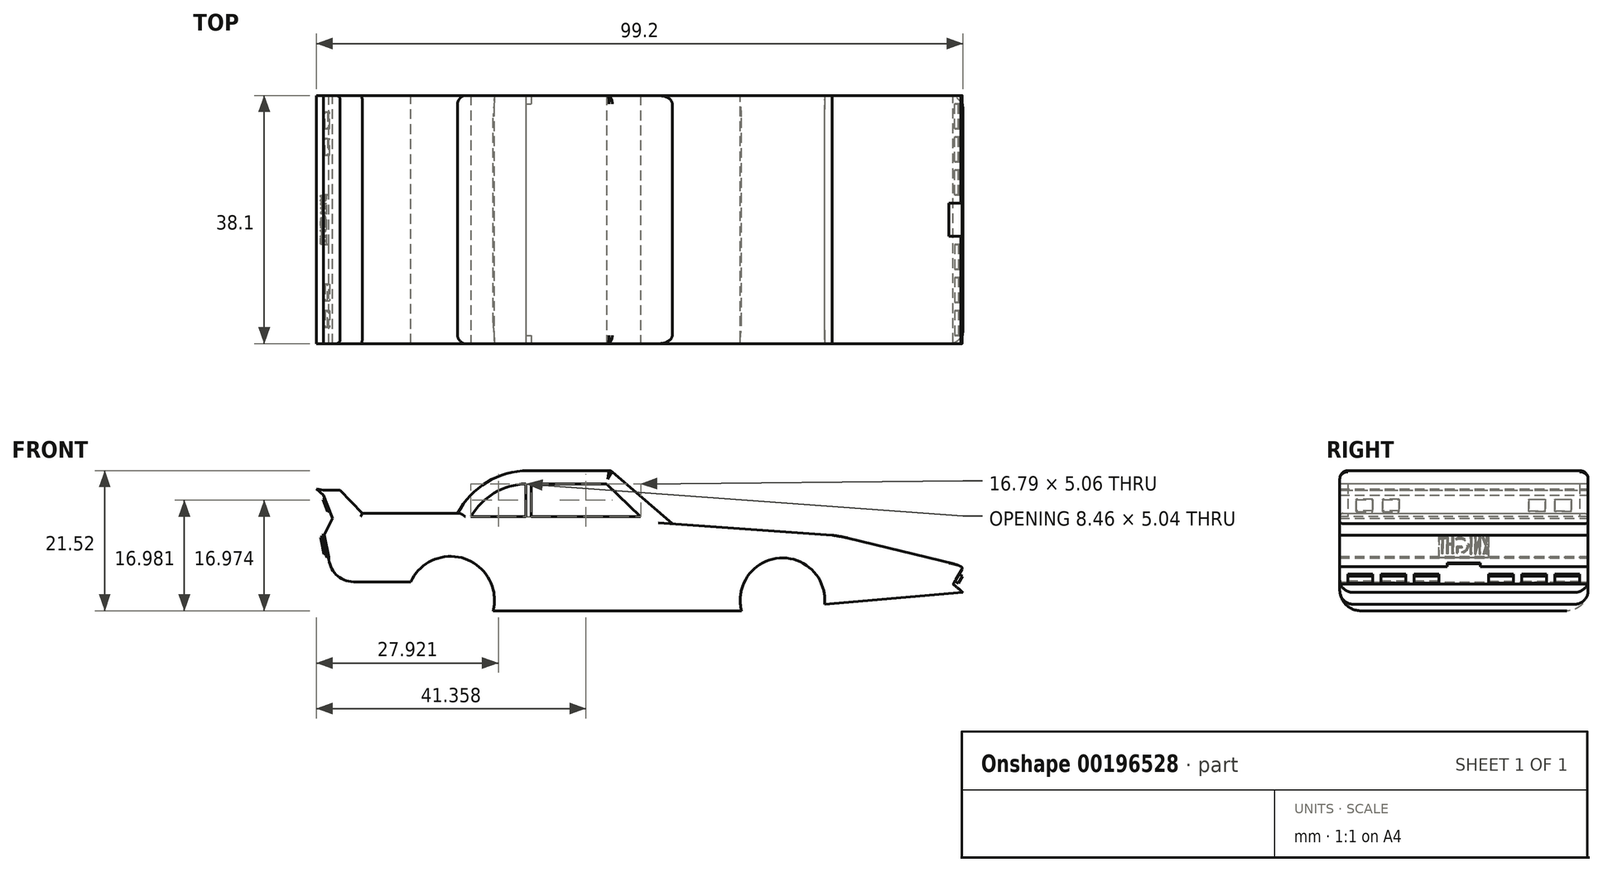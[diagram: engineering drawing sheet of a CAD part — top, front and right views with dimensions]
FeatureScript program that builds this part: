
annotation { "Feature Type Name" : "Feature", "Feature Type Description" : "" }
export const myFeature = defineFeature(function(context is Context, id is Id, definition is map)
    precondition{}
    {
        {
            var Q0;
            Q0=qCreatedBy(makeId("Front.planeOp"),FACE);
            var sketch = newSketch(context, id + "F0", { "sketchPlane" : qUnion([Q0])});
            skArc(sketch, "E0", {"start": v(4.2, 1) * mm, "mid": v(-2.78, 8.1) * mm, "end": v(-8.56, 0) * mm});
            skLineSegment(sketch, "E1", {"start": v(-8.56, 0) * mm, "end": v(-46.66, 0) * mm});
            skArc(sketch, "E2", {"start": v(-46.66, 0) * mm, "mid": v(-50.95, 7.97) * mm, "end": v(-59.3, 4.46) * mm});
            skLineSegment(sketch, "E3", {"start": v(-59.3, 4.46) * mm, "end": v(-68.07, 4.46) * mm});
            skLineSegment(sketch, "E4", {"start": v(-71.88, 8.27) * mm, "end": v(-72.57, 11.67) * mm});
            skLineSegment(sketch, "E5", {"start": v(-72.7, 18.5) * mm, "end": v(-70.16, 18.5) * mm});
            skLineSegment(sketch, "E6", {"start": v(-70.16, 18.5) * mm, "end": v(-66.76, 14.96) * mm});
            skLineSegment(sketch, "E7", {"start": v(-66.76, 14.96) * mm, "end": v(-52.11, 14.96) * mm});
            skLineSegment(sketch, "E8", {"start": v(-41.3, 21.52) * mm, "end": v(-28.6, 21.52) * mm});
            skArc(sketch, "E9", {"start": v(-41.3, 21.52) * mm, "mid": v(-47.62, 19.75) * mm, "end": v(-52.11, 14.96) * mm});
            skLineSegment(sketch, "E10", {"start": v(-28.6, 21.52) * mm, "end": v(-19.19, 13.37) * mm});
            skLineSegment(sketch, "E11", {"start": v(-19.19, 13.37) * mm, "end": v(5.34, 11.62) * mm});
            skLineSegment(sketch, "E12", {"start": v(5.34, 11.62) * mm, "end": v(25.42, 6.72) * mm});
            skLineSegment(sketch, "E13", {"start": v(25.42, 2.81) * mm, "end": v(4.2, 1) * mm});
            skLineSegment(sketch, "E14", {"start": v(25.42, 6.72) * mm, "end": v(23.91, 4.1) * mm});
            skLineSegment(sketch, "E15", {"start": v(23.91, 4.1) * mm, "end": v(25.42, 2.81) * mm});
            skPoint(sketch, "E16.visualSharp", {"position": v(-71.88, 4.46) * mm});
            skArc(sketch, "E16.filletArc", {"start": v(-71.88, 8.27) * mm, "mid": v(-70.77, 5.57) * mm, "end": v(-68.07, 4.46) * mm});
            skPoint(sketch, "E17.orphan", {"position": v(-59.72, 0) * mm});
            skPoint(sketch, "E18.orphan", {"position": v(4.02, 0) * mm});
            skLineSegment(sketch, "E19", {"start": v(-72.7, 18.5) * mm, "end": v(-73.78, 18.73) * mm});
            skLineSegment(sketch, "E20", {"start": v(-73.78, 18.73) * mm, "end": v(-72.7, 17.78) * mm});
            skLineSegment(sketch, "E21", {"start": v(-72.57, 11.67) * mm, "end": v(-71.32, 14.18) * mm});
            skLineSegment(sketch, "E22", {"start": v(-71.32, 14.18) * mm, "end": v(-72.7, 17.78) * mm});
            skSolve(sketch);
        }
        {
            var Q0;
            Q0=makeQuery(id+"F0.imprint","IMPRINT",FACE,{"disambiguationData":[TD([[makeQuery(id+"F0.imprint","IMPRINT",EDGE,{"derivedFrom":sQuery(id+"F0.wireOp",EDGE,"E0")}),-1.0]])]});
            extrude(context, id + "F1", {"entities" : qUnion([Q0]), "endBound" : BoundingType.SYMMETRIC, "depth" : 38.1 * mm});
        }
        {
            var Q0;
            {var subQ0=sQuery(id+"F0.wireOp",EDGE,"piWAozd6-odN5-IXnD-0DmP-VUwjhF2xC87r");var subQ1=sQuery(id+"F0.wireOp",EDGE,"E12");Q0=makeQuery(id+"FV3Uu7cO5sznl1Z_1.boolean.opBoolean","SPLIT",EDGE,{"disambiguationData":[TD([makeQuery(id+"FV3Uu7cO5sznl1Z_1.opExtrude","SWEPT_FACE",FACE,{"disambiguationData":[OSD([sQuery(id+"F6OuYayMSvIZY2Q_1.wireOp",EDGE,"LOxPacLx-S5zq-svhU-HEBB-QED5wKVLpIEs.right")])]})])],"derivedFrom":makeQuery(id+"F1.opExtrude","SWEPT_EDGE",EDGE,{"disambiguationData":[OSD([subQ1,subQ0])]})});}
            var Q1;
            Q1=makeQuery(id+"FV3Uu7cO5sznl1Z_1.boolean.opBoolean","INTERSECT",EDGE,{"derivedFrom":[makeQuery(id+"F1.opExtrude","SWEPT_FACE",FACE,{"disambiguationData":[OSD([sQuery(id+"F0.wireOp",EDGE,"piWAozd6-odN5-IXnD-0DmP-VUwjhF2xC87r")])]}),makeQuery(id+"FV3Uu7cO5sznl1Z_1.opExtrude","CAP_FACE",FACE,{"disambiguationData":[OSD([sQuery(id+"F6OuYayMSvIZY2Q_1.wireOp",EDGE,"LOxPacLx-S5zq-svhU-HEBB-QED5wKVLpIEs.bottom"),sQuery(id+"F6OuYayMSvIZY2Q_1.wireOp",EDGE,"LOxPacLx-S5zq-svhU-HEBB-QED5wKVLpIEs.top"),sQuery(id+"F6OuYayMSvIZY2Q_1.wireOp",EDGE,"LOxPacLx-S5zq-svhU-HEBB-QED5wKVLpIEs.left"),sQuery(id+"F6OuYayMSvIZY2Q_1.wireOp",EDGE,"LOxPacLx-S5zq-svhU-HEBB-QED5wKVLpIEs.right")])],"isStart":false})]});
            var Q2;
            {var subQ0=sQuery(id+"F0.wireOp",EDGE,"E12");var subQ1=sQuery(id+"F0.wireOp",EDGE,"piWAozd6-odN5-IXnD-0DmP-VUwjhF2xC87r");Q2=makeQuery(id+"FV3Uu7cO5sznl1Z_1.boolean.opBoolean","SPLIT",EDGE,{"disambiguationData":[TD([makeQuery(id+"FV3Uu7cO5sznl1Z_1.opExtrude","SWEPT_FACE",FACE,{"disambiguationData":[OSD([sQuery(id+"F6OuYayMSvIZY2Q_1.wireOp",EDGE,"r52KYWLg-ahqb-8f3H-ltxH-kNGmeAsnRNuQ.right")])]})])],"derivedFrom":makeQuery(id+"F1.opExtrude","SWEPT_EDGE",EDGE,{"disambiguationData":[OSD([subQ0,subQ1])]})});}
            var Q3;
            Q3=makeQuery(id+"FV3Uu7cO5sznl1Z_1.boolean.opBoolean","INTERSECT",EDGE,{"derivedFrom":[makeQuery(id+"F1.opExtrude","SWEPT_FACE",FACE,{"disambiguationData":[OSD([sQuery(id+"F0.wireOp",EDGE,"piWAozd6-odN5-IXnD-0DmP-VUwjhF2xC87r")])]}),makeQuery(id+"FV3Uu7cO5sznl1Z_1.opExtrude","CAP_FACE",FACE,{"disambiguationData":[OSD([sQuery(id+"F6OuYayMSvIZY2Q_1.wireOp",EDGE,"r52KYWLg-ahqb-8f3H-ltxH-kNGmeAsnRNuQ.bottom"),sQuery(id+"F6OuYayMSvIZY2Q_1.wireOp",EDGE,"r52KYWLg-ahqb-8f3H-ltxH-kNGmeAsnRNuQ.top"),sQuery(id+"F6OuYayMSvIZY2Q_1.wireOp",EDGE,"r52KYWLg-ahqb-8f3H-ltxH-kNGmeAsnRNuQ.left"),sQuery(id+"F6OuYayMSvIZY2Q_1.wireOp",EDGE,"r52KYWLg-ahqb-8f3H-ltxH-kNGmeAsnRNuQ.right")])],"isStart":false})]});
            var Q4;
            {var subQ0=sQuery(id+"F0.wireOp",EDGE,"E12");var subQ1=sQuery(id+"F0.wireOp",EDGE,"piWAozd6-odN5-IXnD-0DmP-VUwjhF2xC87r");Q4=makeQuery(id+"FV3Uu7cO5sznl1Z_1.boolean.opBoolean","SPLIT",EDGE,{"disambiguationData":[TD([makeQuery(id+"FV3Uu7cO5sznl1Z_1.opExtrude","SWEPT_FACE",FACE,{"disambiguationData":[OSD([sQuery(id+"F6OuYayMSvIZY2Q_1.wireOp",EDGE,"NTCnOCoN-yu8C-SXyQ-er5I-QvQ5yvy4iVEx.right")])]})])],"derivedFrom":makeQuery(id+"F1.opExtrude","SWEPT_EDGE",EDGE,{"disambiguationData":[OSD([subQ0,subQ1])]})});}
            var Q5;
            Q5=makeQuery(id+"FV3Uu7cO5sznl1Z_1.boolean.opBoolean","INTERSECT",EDGE,{"derivedFrom":[makeQuery(id+"F1.opExtrude","SWEPT_FACE",FACE,{"disambiguationData":[OSD([sQuery(id+"F0.wireOp",EDGE,"piWAozd6-odN5-IXnD-0DmP-VUwjhF2xC87r")])]}),makeQuery(id+"FV3Uu7cO5sznl1Z_1.opExtrude","CAP_FACE",FACE,{"disambiguationData":[OSD([sQuery(id+"F6OuYayMSvIZY2Q_1.wireOp",EDGE,"NTCnOCoN-yu8C-SXyQ-er5I-QvQ5yvy4iVEx.bottom"),sQuery(id+"F6OuYayMSvIZY2Q_1.wireOp",EDGE,"NTCnOCoN-yu8C-SXyQ-er5I-QvQ5yvy4iVEx.top"),sQuery(id+"F6OuYayMSvIZY2Q_1.wireOp",EDGE,"NTCnOCoN-yu8C-SXyQ-er5I-QvQ5yvy4iVEx.left"),sQuery(id+"F6OuYayMSvIZY2Q_1.wireOp",EDGE,"NTCnOCoN-yu8C-SXyQ-er5I-QvQ5yvy4iVEx.right")])],"isStart":false})]});
            var Q6;
            {var subQ0=sQuery(id+"F0.wireOp",EDGE,"E12");var subQ1=sQuery(id+"F0.wireOp",EDGE,"piWAozd6-odN5-IXnD-0DmP-VUwjhF2xC87r");Q6=makeQuery(id+"FV3Uu7cO5sznl1Z_1.boolean.opBoolean","SPLIT",EDGE,{"disambiguationData":[TD([makeQuery(id+"FV3Uu7cO5sznl1Z_1.opExtrude","SWEPT_FACE",FACE,{"disambiguationData":[OSD([sQuery(id+"F6OuYayMSvIZY2Q_1.wireOp",EDGE,"9fj7zr7S-9n9s-cSpx-WFiQ-eEYzpOB873Fi.right")])]})])],"derivedFrom":makeQuery(id+"F1.opExtrude","SWEPT_EDGE",EDGE,{"disambiguationData":[OSD([subQ0,subQ1])]})});}
            var Q7;
            Q7=makeQuery(id+"FV3Uu7cO5sznl1Z_1.boolean.opBoolean","INTERSECT",EDGE,{"derivedFrom":[makeQuery(id+"F1.opExtrude","SWEPT_FACE",FACE,{"disambiguationData":[OSD([sQuery(id+"F0.wireOp",EDGE,"piWAozd6-odN5-IXnD-0DmP-VUwjhF2xC87r")])]}),makeQuery(id+"FV3Uu7cO5sznl1Z_1.opExtrude","CAP_FACE",FACE,{"disambiguationData":[OSD([sQuery(id+"F6OuYayMSvIZY2Q_1.wireOp",EDGE,"9fj7zr7S-9n9s-cSpx-WFiQ-eEYzpOB873Fi.bottom"),sQuery(id+"F6OuYayMSvIZY2Q_1.wireOp",EDGE,"9fj7zr7S-9n9s-cSpx-WFiQ-eEYzpOB873Fi.top"),sQuery(id+"F6OuYayMSvIZY2Q_1.wireOp",EDGE,"9fj7zr7S-9n9s-cSpx-WFiQ-eEYzpOB873Fi.left"),sQuery(id+"F6OuYayMSvIZY2Q_1.wireOp",EDGE,"9fj7zr7S-9n9s-cSpx-WFiQ-eEYzpOB873Fi.right")])],"isStart":false})]});
            var Q8;
            {var subQ0=sQuery(id+"F0.wireOp",EDGE,"E12");var subQ1=sQuery(id+"F0.wireOp",EDGE,"piWAozd6-odN5-IXnD-0DmP-VUwjhF2xC87r");Q8=makeQuery(id+"FV3Uu7cO5sznl1Z_1.boolean.opBoolean","SPLIT",EDGE,{"disambiguationData":[TD([makeQuery(id+"FV3Uu7cO5sznl1Z_1.opExtrude","SWEPT_FACE",FACE,{"disambiguationData":[OSD([sQuery(id+"F6OuYayMSvIZY2Q_1.wireOp",EDGE,"LBPB0bUL-G7kI-9L5E-pr7f-Sai9KsrLVXPn.right")])]})])],"derivedFrom":makeQuery(id+"F1.opExtrude","SWEPT_EDGE",EDGE,{"disambiguationData":[OSD([subQ0,subQ1])]})});}
            var Q9;
            Q9=makeQuery(id+"FV3Uu7cO5sznl1Z_1.boolean.opBoolean","INTERSECT",EDGE,{"derivedFrom":[makeQuery(id+"F1.opExtrude","SWEPT_FACE",FACE,{"disambiguationData":[OSD([sQuery(id+"F0.wireOp",EDGE,"piWAozd6-odN5-IXnD-0DmP-VUwjhF2xC87r")])]}),makeQuery(id+"FV3Uu7cO5sznl1Z_1.opExtrude","CAP_FACE",FACE,{"disambiguationData":[OSD([sQuery(id+"F6OuYayMSvIZY2Q_1.wireOp",EDGE,"LBPB0bUL-G7kI-9L5E-pr7f-Sai9KsrLVXPn.bottom"),sQuery(id+"F6OuYayMSvIZY2Q_1.wireOp",EDGE,"LBPB0bUL-G7kI-9L5E-pr7f-Sai9KsrLVXPn.top"),sQuery(id+"F6OuYayMSvIZY2Q_1.wireOp",EDGE,"LBPB0bUL-G7kI-9L5E-pr7f-Sai9KsrLVXPn.left"),sQuery(id+"F6OuYayMSvIZY2Q_1.wireOp",EDGE,"LBPB0bUL-G7kI-9L5E-pr7f-Sai9KsrLVXPn.right")])],"isStart":false})]});
            var Q10;
            {var subQ0=sQuery(id+"F0.wireOp",EDGE,"E12");var subQ1=sQuery(id+"F0.wireOp",EDGE,"piWAozd6-odN5-IXnD-0DmP-VUwjhF2xC87r");Q10=makeQuery(id+"FV3Uu7cO5sznl1Z_1.boolean.opBoolean","SPLIT",EDGE,{"disambiguationData":[TD([makeQuery(id+"FV3Uu7cO5sznl1Z_1.opExtrude","SWEPT_FACE",FACE,{"disambiguationData":[OSD([sQuery(id+"F6OuYayMSvIZY2Q_1.wireOp",EDGE,"LBPB0bUL-G7kI-9L5E-pr7f-Sai9KsrLVXPn.left")])]})])],"derivedFrom":makeQuery(id+"F1.opExtrude","SWEPT_EDGE",EDGE,{"disambiguationData":[OSD([subQ0,subQ1])]})});}
            var Q11;
            Q11=makeQuery(id+"FV3Uu7cO5sznl1Z_1.boolean.opBoolean","INTERSECT",EDGE,{"derivedFrom":[makeQuery(id+"F1.opExtrude","SWEPT_FACE",FACE,{"disambiguationData":[OSD([sQuery(id+"F0.wireOp",EDGE,"piWAozd6-odN5-IXnD-0DmP-VUwjhF2xC87r")])]}),makeQuery(id+"FV3Uu7cO5sznl1Z_1.opExtrude","CAP_FACE",FACE,{"disambiguationData":[OSD([sQuery(id+"F6OuYayMSvIZY2Q_1.wireOp",EDGE,"508af859-bfde-4d98-a90f-149fa62f811b0.MirrorCS"),sQuery(id+"F6OuYayMSvIZY2Q_1.wireOp",EDGE,"37228f31-ebda-4232-9122-c2d6d20dc8920.MirrorCS"),sQuery(id+"F6OuYayMSvIZY2Q_1.wireOp",EDGE,"360aa123-8f3f-4f13-a378-a52a7b43db5a0.MirrorCS"),sQuery(id+"F6OuYayMSvIZY2Q_1.wireOp",EDGE,"0596e637-3ff4-463e-845c-65e150e65c670.MirrorCS")])],"isStart":false})]});
            var Q12;
            {var subQ0=sQuery(id+"F0.wireOp",EDGE,"E12");var subQ1=sQuery(id+"F0.wireOp",EDGE,"piWAozd6-odN5-IXnD-0DmP-VUwjhF2xC87r");Q12=makeQuery(id+"FV3Uu7cO5sznl1Z_1.boolean.opBoolean","SPLIT",EDGE,{"disambiguationData":[TD([makeQuery(id+"FV3Uu7cO5sznl1Z_1.opExtrude","SWEPT_FACE",FACE,{"disambiguationData":[OSD([sQuery(id+"F6OuYayMSvIZY2Q_1.wireOp",EDGE,"360aa123-8f3f-4f13-a378-a52a7b43db5a0.MirrorCS")])]})])],"derivedFrom":makeQuery(id+"F1.opExtrude","SWEPT_EDGE",EDGE,{"disambiguationData":[OSD([subQ0,subQ1])]})});}
            var Q13;
            Q13=makeQuery(id+"FV3Uu7cO5sznl1Z_1.boolean.opBoolean","INTERSECT",EDGE,{"derivedFrom":[makeQuery(id+"F1.opExtrude","SWEPT_FACE",FACE,{"disambiguationData":[OSD([sQuery(id+"F0.wireOp",EDGE,"piWAozd6-odN5-IXnD-0DmP-VUwjhF2xC87r")])]}),makeQuery(id+"FV3Uu7cO5sznl1Z_1.opExtrude","CAP_FACE",FACE,{"disambiguationData":[OSD([sQuery(id+"F6OuYayMSvIZY2Q_1.wireOp",EDGE,"bb352b80-0b1b-409d-a26b-4e7a8cd47cef0.MirrorCS"),sQuery(id+"F6OuYayMSvIZY2Q_1.wireOp",EDGE,"cf446a10-7582-4012-8e6f-7b8a887e3fab0.MirrorCS"),sQuery(id+"F6OuYayMSvIZY2Q_1.wireOp",EDGE,"d08ecadf-17e7-492c-b659-bda2cb3b14340.MirrorCS"),sQuery(id+"F6OuYayMSvIZY2Q_1.wireOp",EDGE,"e908241f-848e-4f62-8962-ae2c5000804a0.MirrorCS")])],"isStart":false})]});
            var Q14;
            {var subQ0=sQuery(id+"F0.wireOp",EDGE,"E12");var subQ1=sQuery(id+"F0.wireOp",EDGE,"piWAozd6-odN5-IXnD-0DmP-VUwjhF2xC87r");Q14=makeQuery(id+"FV3Uu7cO5sznl1Z_1.boolean.opBoolean","SPLIT",EDGE,{"disambiguationData":[TD([makeQuery(id+"FV3Uu7cO5sznl1Z_1.opExtrude","SWEPT_FACE",FACE,{"disambiguationData":[OSD([sQuery(id+"F6OuYayMSvIZY2Q_1.wireOp",EDGE,"cf446a10-7582-4012-8e6f-7b8a887e3fab0.MirrorCS")])]})])],"derivedFrom":makeQuery(id+"F1.opExtrude","SWEPT_EDGE",EDGE,{"disambiguationData":[OSD([subQ0,subQ1])]})});}
            var Q15;
            Q15=makeQuery(id+"FV3Uu7cO5sznl1Z_1.boolean.opBoolean","INTERSECT",EDGE,{"derivedFrom":[makeQuery(id+"F1.opExtrude","SWEPT_FACE",FACE,{"disambiguationData":[OSD([sQuery(id+"F0.wireOp",EDGE,"piWAozd6-odN5-IXnD-0DmP-VUwjhF2xC87r")])]}),makeQuery(id+"FV3Uu7cO5sznl1Z_1.opExtrude","CAP_FACE",FACE,{"disambiguationData":[OSD([sQuery(id+"F6OuYayMSvIZY2Q_1.wireOp",EDGE,"8a9b0b0e-97b4-4ba9-a973-1c92080a53030.MirrorCS"),sQuery(id+"F6OuYayMSvIZY2Q_1.wireOp",EDGE,"3b6446a7-c2c3-40b9-9697-2142afb4b24a0.MirrorCS"),sQuery(id+"F6OuYayMSvIZY2Q_1.wireOp",EDGE,"c94ae0a3-7226-48b3-982c-0a8c260cbade0.MirrorCS"),sQuery(id+"F6OuYayMSvIZY2Q_1.wireOp",EDGE,"839fec6f-e18f-459d-ad96-e984b2c5d6d60.MirrorCS")])],"isStart":false})]});
            var Q16;
            {var subQ0=sQuery(id+"F0.wireOp",EDGE,"E12");var subQ1=sQuery(id+"F0.wireOp",EDGE,"piWAozd6-odN5-IXnD-0DmP-VUwjhF2xC87r");Q16=makeQuery(id+"FV3Uu7cO5sznl1Z_1.boolean.opBoolean","SPLIT",EDGE,{"disambiguationData":[TD([makeQuery(id+"FV3Uu7cO5sznl1Z_1.opExtrude","SWEPT_FACE",FACE,{"disambiguationData":[OSD([sQuery(id+"F6OuYayMSvIZY2Q_1.wireOp",EDGE,"839fec6f-e18f-459d-ad96-e984b2c5d6d60.MirrorCS")])]})])],"derivedFrom":makeQuery(id+"F1.opExtrude","SWEPT_EDGE",EDGE,{"disambiguationData":[OSD([subQ0,subQ1])]})});}
            var Q17;
            Q17=makeQuery(id+"FV3Uu7cO5sznl1Z_1.boolean.opBoolean","INTERSECT",EDGE,{"derivedFrom":[makeQuery(id+"F1.opExtrude","SWEPT_FACE",FACE,{"disambiguationData":[OSD([sQuery(id+"F0.wireOp",EDGE,"piWAozd6-odN5-IXnD-0DmP-VUwjhF2xC87r")])]}),makeQuery(id+"FV3Uu7cO5sznl1Z_1.opExtrude","CAP_FACE",FACE,{"disambiguationData":[OSD([sQuery(id+"F6OuYayMSvIZY2Q_1.wireOp",EDGE,"05967368-317e-4f26-8281-6c34b3c6d1e60.MirrorCS"),sQuery(id+"F6OuYayMSvIZY2Q_1.wireOp",EDGE,"10d03c6d-404a-41d4-ac66-de4be596f0e30.MirrorCS"),sQuery(id+"F6OuYayMSvIZY2Q_1.wireOp",EDGE,"09338377-e241-4c4c-a4fa-bf4e565ec6370.MirrorCS"),sQuery(id+"F6OuYayMSvIZY2Q_1.wireOp",EDGE,"4262b961-d854-423d-87d7-c21d2e8108a90.MirrorCS")])],"isStart":false})]});
            var Q18;
            {var subQ0=sQuery(id+"F0.wireOp",EDGE,"E12");var subQ1=sQuery(id+"F0.wireOp",EDGE,"piWAozd6-odN5-IXnD-0DmP-VUwjhF2xC87r");Q18=makeQuery(id+"FV3Uu7cO5sznl1Z_1.boolean.opBoolean","SPLIT",EDGE,{"disambiguationData":[TD([makeQuery(id+"FV3Uu7cO5sznl1Z_1.opExtrude","SWEPT_FACE",FACE,{"disambiguationData":[OSD([sQuery(id+"F6OuYayMSvIZY2Q_1.wireOp",EDGE,"10d03c6d-404a-41d4-ac66-de4be596f0e30.MirrorCS")])]})])],"derivedFrom":makeQuery(id+"F1.opExtrude","SWEPT_EDGE",EDGE,{"disambiguationData":[OSD([subQ0,subQ1])]})});}
            var Q19;
            Q19=makeQuery(id+"FV3Uu7cO5sznl1Z_1.boolean.opBoolean","INTERSECT",EDGE,{"derivedFrom":[makeQuery(id+"F1.opExtrude","SWEPT_FACE",FACE,{"disambiguationData":[OSD([sQuery(id+"F0.wireOp",EDGE,"piWAozd6-odN5-IXnD-0DmP-VUwjhF2xC87r")])]}),makeQuery(id+"FV3Uu7cO5sznl1Z_1.opExtrude","CAP_FACE",FACE,{"disambiguationData":[OSD([sQuery(id+"F6OuYayMSvIZY2Q_1.wireOp",EDGE,"74e5a05d-e68e-48eb-8f2f-b1d45a82cd280.MirrorCS"),sQuery(id+"F6OuYayMSvIZY2Q_1.wireOp",EDGE,"93f09404-d1ae-43cb-bdeb-6ca15733254d0.MirrorCS"),sQuery(id+"F6OuYayMSvIZY2Q_1.wireOp",EDGE,"a1cbbde3-3219-4e6b-ba27-ff48f55d945b0.MirrorCS"),sQuery(id+"F6OuYayMSvIZY2Q_1.wireOp",EDGE,"cdac1700-6b11-4df6-9001-883cc821f1520.MirrorCS")])],"isStart":false})]});
            var Q20;
            {var subQ0=sQuery(id+"F0.wireOp",EDGE,"piWAozd6-odN5-IXnD-0DmP-VUwjhF2xC87r");var subQ1=sQuery(id+"F0.wireOp",EDGE,"E12");Q20=makeQuery(id+"FV3Uu7cO5sznl1Z_1.boolean.opBoolean","SPLIT",EDGE,{"disambiguationData":[TD([makeQuery(id+"FV3Uu7cO5sznl1Z_1.opExtrude","SWEPT_FACE",FACE,{"disambiguationData":[OSD([sQuery(id+"F6OuYayMSvIZY2Q_1.wireOp",EDGE,"a1cbbde3-3219-4e6b-ba27-ff48f55d945b0.MirrorCS")])]})])],"derivedFrom":makeQuery(id+"F1.opExtrude","SWEPT_EDGE",EDGE,{"disambiguationData":[OSD([subQ1,subQ0])]})});}
            fillet(context, id + "F2", {"entities" : qUnion([Q0, Q1, Q2, Q3, Q4, Q5, Q6, Q7, Q8, Q9, Q10, Q11, Q12, Q13, Q14, Q15, Q16, Q17, Q18, Q19, Q20]), "radius" : 0.25 * mm, "tangentPropagation" : true, "allowEdgeOverflow" : false});
        }
        {
            var Q0;
            Q0=makeQuery(id+"F1.opExtrude","SWEPT_FACE",FACE,{"disambiguationData":[OSD([sQuery(id+"F0.wireOp",EDGE,"E14")])]});
            var sketch = newSketch(context, id + "F3", { "sketchPlane" : qUnion([Q0])});
            skLineSegment(sketch, "E23", {"start": v(0, 18.14) * mm, "end": v(0, 15.46) * mm});
            skLineSegment(sketch, "E24", {"start": v(0, 18.14) * mm, "end": v(-3.81, 18.14) * mm});
            skLineSegment(sketch, "E25.bottom", {"start": v(-3.81, 17.24) * mm, "end": v(-7.62, 17.24) * mm});
            skLineSegment(sketch, "E25.top", {"start": v(-3.8, 15.97) * mm, "end": v(-7.62, 15.97) * mm});
            skLineSegment(sketch, "E25.left", {"start": v(-3.8, 17.24) * mm, "end": v(-3.8, 15.97) * mm});
            skLineSegment(sketch, "E25.right", {"start": v(-7.62, 17.24) * mm, "end": v(-7.62, 15.97) * mm});
            skLineSegment(sketch, "E26.bottom", {"start": v(-8.9, 17.24) * mm, "end": v(-12.7, 17.24) * mm});
            skLineSegment(sketch, "E26.top", {"start": v(-8.89, 15.97) * mm, "end": v(-12.7, 15.97) * mm});
            skLineSegment(sketch, "E26.left", {"start": v(-8.9, 17.24) * mm, "end": v(-8.89, 15.97) * mm});
            skLineSegment(sketch, "E26.right", {"start": v(-12.7, 17.24) * mm, "end": v(-12.7, 15.97) * mm});
            skLineSegment(sketch, "E27.bottom", {"start": v(-13.97, 17.24) * mm, "end": v(-17.78, 17.24) * mm});
            skLineSegment(sketch, "E27.top", {"start": v(-13.97, 15.97) * mm, "end": v(-17.78, 15.97) * mm});
            skLineSegment(sketch, "E27.left", {"start": v(-13.97, 17.24) * mm, "end": v(-13.97, 15.97) * mm});
            skLineSegment(sketch, "E27.right", {"start": v(-17.78, 17.24) * mm, "end": v(-17.78, 15.97) * mm});
            skLineSegment(sketch, "E28.MirrorCS", {"start": v(3.81, 17.24) * mm, "end": v(7.62, 17.24) * mm});
            skLineSegment(sketch, "E29.MirrorCS", {"start": v(3.8, 17.24) * mm, "end": v(3.8, 15.97) * mm});
            skLineSegment(sketch, "E30.MirrorCS", {"start": v(3.81, 15.97) * mm, "end": v(7.62, 15.97) * mm});
            skLineSegment(sketch, "E31.MirrorCS", {"start": v(7.62, 17.24) * mm, "end": v(7.62, 15.97) * mm});
            skLineSegment(sketch, "E32.MirrorCS", {"start": v(8.9, 17.24) * mm, "end": v(8.9, 15.97) * mm});
            skLineSegment(sketch, "E33.MirrorCS", {"start": v(8.9, 17.24) * mm, "end": v(12.7, 17.24) * mm});
            skLineSegment(sketch, "E34.MirrorCS", {"start": v(8.89, 15.97) * mm, "end": v(12.7, 15.97) * mm});
            skLineSegment(sketch, "E35.MirrorCS", {"start": v(12.7, 17.24) * mm, "end": v(12.7, 15.97) * mm});
            skLineSegment(sketch, "E36.MirrorCS", {"start": v(13.97, 17.24) * mm, "end": v(13.97, 15.97) * mm});
            skLineSegment(sketch, "E37.MirrorCS", {"start": v(13.97, 17.24) * mm, "end": v(17.78, 17.24) * mm});
            skLineSegment(sketch, "E38.MirrorCS", {"start": v(17.78, 17.24) * mm, "end": v(17.78, 15.97) * mm});
            skLineSegment(sketch, "E39.MirrorCS", {"start": v(13.97, 15.97) * mm, "end": v(17.78, 15.97) * mm});
            skSolve(sketch);
        }
        {
            var Q0;
            Q0=makeQuery(id+"F3.imprint","IMPRINT",FACE,{"disambiguationData":[TD([[makeQuery(id+"F3.imprint","IMPRINT",EDGE,{"derivedFrom":sQuery(id+"F3.wireOp",EDGE,"E27.bottom")}),1.0]])]});
            var Q1;
            Q1=makeQuery(id+"F3.imprint","IMPRINT",FACE,{"disambiguationData":[TD([[makeQuery(id+"F3.imprint","IMPRINT",EDGE,{"derivedFrom":sQuery(id+"F3.wireOp",EDGE,"E26.bottom")}),1.0]])]});
            var Q2;
            Q2=makeQuery(id+"F3.imprint","IMPRINT",FACE,{"disambiguationData":[TD([[makeQuery(id+"F3.imprint","IMPRINT",EDGE,{"derivedFrom":sQuery(id+"F3.wireOp",EDGE,"E25.bottom")}),1.0]])]});
            var Q3;
            Q3=makeQuery(id+"F3.imprint","IMPRINT",FACE,{"disambiguationData":[TD([[makeQuery(id+"F3.imprint","IMPRINT",EDGE,{"derivedFrom":sQuery(id+"F3.wireOp",EDGE,"E28.MirrorCS")}),-1.0]])]});
            var Q4;
            Q4=makeQuery(id+"F3.imprint","IMPRINT",FACE,{"disambiguationData":[TD([[makeQuery(id+"F3.imprint","IMPRINT",EDGE,{"derivedFrom":sQuery(id+"F3.wireOp",EDGE,"E32.MirrorCS")}),1.0]])]});
            var Q5;
            Q5=makeQuery(id+"F3.imprint","IMPRINT",FACE,{"disambiguationData":[TD([[makeQuery(id+"F3.imprint","IMPRINT",EDGE,{"derivedFrom":sQuery(id+"F3.wireOp",EDGE,"E36.MirrorCS")}),1.0]])]});
            extrude(context, id + "F4", {"entities" : qUnion([Q0, Q1, Q2, Q3, Q4, Q5]), "operationType" : NewBodyOperationType.ADD, "endBound" : BoundingType.SYMMETRIC, "oppositeDirection" : true, "depth" : 1.27 * mm});
        }
        {
            var Q0;
            Q0=makeQuery(id+"F1.opExtrude","SWEPT_FACE",FACE,{"disambiguationData":[OSD([sQuery(id+"F0.wireOp",EDGE,"E12")])]});
            var sketch = newSketch(context, id + "F5", { "sketchPlane" : qUnion([Q0])});
            skLineSegment(sketch, "E40.bottom", {"start": v(22.76, -2.54) * mm, "end": v(20.86, -2.54) * mm});
            skLineSegment(sketch, "E40.top", {"start": v(22.76, 2.54) * mm, "end": v(20.86, 2.54) * mm});
            skLineSegment(sketch, "E40.left", {"start": v(22.76, -2.54) * mm, "end": v(22.76, 2.54) * mm});
            skLineSegment(sketch, "E40.right", {"start": v(20.86, -2.54) * mm, "end": v(20.86, 2.54) * mm});
            skSolve(sketch);
        }
        {
            var Q0;
            {var subQ4=sQuery(id+"F5.wireOp",EDGE,"E40.bottom");Q0=makeQuery(id+"F5.imprint","IMPRINT",FACE,{"disambiguationData":[TD([[makeQuery(id+"F5.imprint","IMPRINT",EDGE,{"derivedFrom":subQ4}),1.0]])]});}
            extrude(context, id + "F6", {"entities" : qUnion([Q0]), "operationType" : NewBodyOperationType.ADD, "endBound" : BoundingType.SYMMETRIC, "depth" : 0.25 * mm});
        }
        {
            var Q0;
            Q0=makeQuery(id+"F1.opExtrude","CAP_EDGE",EDGE,{"disambiguationData":[OSD([sQuery(id+"F0.wireOp",EDGE,"E8")])],"isStart":true});
            var Q1;
            Q1=makeQuery(id+"F1.opExtrude","CAP_EDGE",EDGE,{"disambiguationData":[OSD([sQuery(id+"F0.wireOp",EDGE,"E8")])],"isStart":false});
            var Q2;
            Q2=makeQuery(id+"F1.opExtrude","CAP_EDGE",EDGE,{"disambiguationData":[OSD([sQuery(id+"F0.wireOp",EDGE,"E10")])],"isStart":false});
            var Q3;
            Q3=makeQuery(id+"F1.opExtrude","CAP_EDGE",EDGE,{"disambiguationData":[OSD([sQuery(id+"F0.wireOp",EDGE,"E10")])],"isStart":true});
            var Q4;
            Q4=makeQuery(id+"F1.opExtrude","CAP_EDGE",EDGE,{"disambiguationData":[OSD([sQuery(id+"F0.wireOp",EDGE,"E9")])],"isStart":false});
            var Q5;
            Q5=makeQuery(id+"F1.opExtrude","CAP_EDGE",EDGE,{"disambiguationData":[OSD([sQuery(id+"F0.wireOp",EDGE,"E9")])],"isStart":true});
            fillet(context, id + "F7", {"entities" : qUnion([Q0, Q1, Q2, Q3, Q4, Q5]), "radius" : 1.27 * mm, "tangentPropagation" : true, "allowEdgeOverflow" : false});
        }
        {
            var Q0;
            Q0=makeQuery(id+"F1.opExtrude","CAP_EDGE",EDGE,{"disambiguationData":[OSD([sQuery(id+"F0.wireOp",EDGE,"E7")])],"isStart":false});
            var Q1;
            Q1=makeQuery(id+"F1.opExtrude","CAP_EDGE",EDGE,{"disambiguationData":[OSD([sQuery(id+"F0.wireOp",EDGE,"E7")])],"isStart":true});
            var Q2;
            Q2=makeQuery(id+"F1.opExtrude","CAP_EDGE",EDGE,{"disambiguationData":[OSD([sQuery(id+"F0.wireOp",EDGE,"E6")])],"isStart":false});
            var Q3;
            Q3=makeQuery(id+"F1.opExtrude","CAP_EDGE",EDGE,{"disambiguationData":[OSD([sQuery(id+"F0.wireOp",EDGE,"E6")])],"isStart":true});
            fillet(context, id + "F8", {"entities" : qUnion([Q0, Q1, Q2, Q3]), "radius" : 0.5 * mm, "tangentPropagation" : true, "allowEdgeOverflow" : false});
        }
        {
            var Q0;
            Q0=makeQuery(id+"F1.opExtrude","SWEPT_FACE",FACE,{"disambiguationData":[OSD([sQuery(id+"F0.wireOp",EDGE,"E22")])]});
            var sketch = newSketch(context, id + "F9", { "sketchPlane" : qUnion([Q0])});
            skLineSegment(sketch, "E41.bottom", {"start": v(-16.51, 41.84) * mm, "end": v(-13.97, 41.84) * mm});
            skLineSegment(sketch, "E41.top", {"start": v(-16.51, 39.94) * mm, "end": v(-13.97, 39.94) * mm});
            skLineSegment(sketch, "E41.left", {"start": v(-16.5, 41.84) * mm, "end": v(-16.5, 39.94) * mm});
            skLineSegment(sketch, "E41.right", {"start": v(-13.97, 41.84) * mm, "end": v(-13.97, 39.94) * mm});
            skLineSegment(sketch, "E42.bottom", {"start": v(-12.47, 39.94) * mm, "end": v(-9.93, 39.94) * mm});
            skLineSegment(sketch, "E42.top", {"start": v(-12.47, 41.84) * mm, "end": v(-9.93, 41.84) * mm});
            skLineSegment(sketch, "E42.left", {"start": v(-12.47, 39.94) * mm, "end": v(-12.47, 41.84) * mm});
            skLineSegment(sketch, "E42.right", {"start": v(-9.93, 39.94) * mm, "end": v(-9.93, 41.84) * mm});
            skLineSegment(sketch, "E43.MirrorCS", {"start": v(9.93, 39.94) * mm, "end": v(9.93, 41.84) * mm});
            skLineSegment(sketch, "E44.MirrorCS", {"start": v(12.47, 41.84) * mm, "end": v(9.93, 41.84) * mm});
            skLineSegment(sketch, "E45.MirrorCS", {"start": v(12.47, 39.94) * mm, "end": v(9.93, 39.94) * mm});
            skLineSegment(sketch, "E46.MirrorCS", {"start": v(12.47, 39.94) * mm, "end": v(12.47, 41.84) * mm});
            skLineSegment(sketch, "E47.MirrorCS", {"start": v(16.51, 41.84) * mm, "end": v(13.97, 41.84) * mm});
            skLineSegment(sketch, "E48.MirrorCS", {"start": v(16.5, 41.84) * mm, "end": v(16.5, 39.94) * mm});
            skLineSegment(sketch, "E49.MirrorCS", {"start": v(16.51, 39.94) * mm, "end": v(13.97, 39.94) * mm});
            skLineSegment(sketch, "E50.MirrorCS", {"start": v(13.97, 41.84) * mm, "end": v(13.97, 39.94) * mm});
            skSolve(sketch);
        }
        {
            var Q0;
            Q0=makeQuery(id+"F9.imprint","IMPRINT",FACE,{"disambiguationData":[TD([[makeQuery(id+"F9.imprint","IMPRINT",EDGE,{"derivedFrom":sQuery(id+"F9.wireOp",EDGE,"E41.bottom")}),-1.0]])]});
            var Q1;
            Q1=makeQuery(id+"F9.imprint","IMPRINT",FACE,{"disambiguationData":[TD([[makeQuery(id+"F9.imprint","IMPRINT",EDGE,{"derivedFrom":sQuery(id+"F9.wireOp",EDGE,"E42.bottom")}),1.0]])]});
            var Q2;
            Q2=makeQuery(id+"F9.imprint","IMPRINT",FACE,{"disambiguationData":[TD([[makeQuery(id+"F9.imprint","IMPRINT",EDGE,{"derivedFrom":sQuery(id+"F9.wireOp",EDGE,"E43.MirrorCS")}),-1.0]])]});
            var Q3;
            Q3=makeQuery(id+"F9.imprint","IMPRINT",FACE,{"disambiguationData":[TD([[makeQuery(id+"F9.imprint","IMPRINT",EDGE,{"derivedFrom":sQuery(id+"F9.wireOp",EDGE,"E47.MirrorCS")}),1.0]])]});
            extrude(context, id + "F10", {"entities" : qUnion([Q0, Q1, Q2, Q3]), "operationType" : NewBodyOperationType.ADD, "endBound" : BoundingType.SYMMETRIC, "depth" : 0.64 * mm});
        }
        {
            var Q0;
            Q0=makeQuery(id+"F1.opExtrude","SWEPT_FACE",FACE,{"disambiguationData":[OSD([sQuery(id+"F0.wireOp",EDGE,"E4")])]});
            var sketch = newSketch(context, id + "F11", { "sketchPlane" : qUnion([Q0])});
            skLineSegment(sketch, "E51", {"start": v(0, 25.76) * mm, "end": v(-3.8, 25.76) * mm});
            skLineSegment(sketch, "E52.bottom", {"start": v(-3.8, 25.76) * mm, "end": v(3.81, 25.76) * mm});
            skLineSegment(sketch, "E52.top", {"start": v(-3.8, 22.3) * mm, "end": v(3.81, 22.3) * mm});
            skLineSegment(sketch, "E52.left", {"start": v(-3.8, 25.76) * mm, "end": v(-3.8, 22.3) * mm});
            skLineSegment(sketch, "E52.right", {"start": v(3.81, 25.76) * mm, "end": v(3.81, 22.3) * mm});
            skSolve(sketch);
        }
        {
            var Q0;
            Q0=makeQuery(id+"F11.imprint","IMPRINT",FACE,{"disambiguationData":[TD([[makeQuery(id+"F11.imprint","IMPRINT",EDGE,{"derivedFrom":sQuery(id+"F11.wireOp",EDGE,"E52.top")}),-1.0]])]});
            extrude(context, id + "F12", {"entities" : qUnion([Q0]), "operationType" : NewBodyOperationType.ADD, "endBound" : BoundingType.SYMMETRIC, "depth" : 0.64 * mm});
        }
        {
            var Q0;
            Q0=makeQuery(id+"F12.opExtrude","CAP_FACE",FACE,{"disambiguationData":[OSD([sQuery(id+"F11.wireOp",EDGE,"E52.bottom"),sQuery(id+"F11.wireOp",EDGE,"E52.top"),sQuery(id+"F11.wireOp",EDGE,"E52.left"),sQuery(id+"F11.wireOp",EDGE,"E52.right")])],"isStart":false});
            var sketch = newSketch(context, id + "F13", { "sketchPlane" : qUnion([Q0])});
            skLineSegment(sketch, "E53", {"start": v(-3.75, 25.5) * mm, "end": v(-3.75, 22.88) * mm});
            skLineSegment(sketch, "E54", {"start": v(-3.75, 22.88) * mm, "end": v(-3.5, 22.88) * mm});
            skLineSegment(sketch, "E55", {"start": v(-3.5, 22.88) * mm, "end": v(-3.5, 24.03) * mm});
            skLineSegment(sketch, "E56", {"start": v(-3.5, 24.03) * mm, "end": v(-3.16, 22.88) * mm});
            skLineSegment(sketch, "E57", {"start": v(-3.16, 22.88) * mm, "end": v(-2.94, 22.88) * mm});
            skLineSegment(sketch, "E58", {"start": v(-3.35, 24.15) * mm, "end": v(-2.83, 25.43) * mm});
            skLineSegment(sketch, "E59", {"start": v(-2.83, 25.43) * mm, "end": v(-3, 25.5) * mm});
            skLineSegment(sketch, "E60", {"start": v(-3, 25.5) * mm, "end": v(-3.5, 24.28) * mm});
            skLineSegment(sketch, "E61", {"start": v(-3.5, 24.28) * mm, "end": v(-3.5, 25.5) * mm});
            skLineSegment(sketch, "E62", {"start": v(-3.5, 25.5) * mm, "end": v(-3.75, 25.5) * mm});
            skLineSegment(sketch, "E63", {"start": v(-2.94, 22.88) * mm, "end": v(-3.35, 24.15) * mm});
            skLineSegment(sketch, "E64", {"start": v(-2.53, 22.88) * mm, "end": v(-2.53, 25.51) * mm});
            skLineSegment(sketch, "E65", {"start": v(-2.53, 25.51) * mm, "end": v(-2.33, 25.51) * mm});
            skLineSegment(sketch, "E66", {"start": v(-2.33, 25.51) * mm, "end": v(-1.84, 23.34) * mm});
            skLineSegment(sketch, "E67", {"start": v(-1.84, 25.51) * mm, "end": v(-1.7, 25.51) * mm});
            skLineSegment(sketch, "E68", {"start": v(-1.7, 25.51) * mm, "end": v(-1.7, 22.88) * mm});
            skLineSegment(sketch, "E69", {"start": v(-1.7, 22.88) * mm, "end": v(-1.84, 22.88) * mm});
            skLineSegment(sketch, "E70", {"start": v(-1.84, 22.88) * mm, "end": v(-2.38, 25.19) * mm});
            skLineSegment(sketch, "E71", {"start": v(-2.38, 25.19) * mm, "end": v(-2.38, 22.88) * mm});
            skLineSegment(sketch, "E72", {"start": v(-2.38, 22.88) * mm, "end": v(-2.53, 22.88) * mm});
            skLineSegment(sketch, "E73.trimOffspring", {"start": v(-1.84, 23.34) * mm, "end": v(-1.84, 25.51) * mm});
            skLineSegment(sketch, "E74", {"start": v(-1.16, 25.47) * mm, "end": v(-0.96, 25.47) * mm});
            skLineSegment(sketch, "E75", {"start": v(-0.96, 25.47) * mm, "end": v(-0.96, 22.88) * mm});
            skLineSegment(sketch, "E76", {"start": v(-0.96, 22.88) * mm, "end": v(-1.15, 22.88) * mm});
            skLineSegment(sketch, "E77", {"start": v(-1.15, 22.88) * mm, "end": v(-1.16, 25.47) * mm});
            skArc(sketch, "E78", {"start": v(1.25, 25.28) * mm, "mid": v(-0.67, 24.25) * mm, "end": v(1.12, 23.01) * mm});
            skLineSegment(sketch, "E79", {"start": v(1.12, 23.01) * mm, "end": v(1.12, 24.02) * mm});
            skLineSegment(sketch, "E80", {"start": v(1.12, 24.02) * mm, "end": v(0.27, 24.02) * mm});
            skLineSegment(sketch, "E81", {"start": v(0.27, 24.02) * mm, "end": v(0.27, 23.83) * mm});
            skLineSegment(sketch, "E82", {"start": v(0.27, 23.83) * mm, "end": v(0.92, 23.83) * mm});
            skLineSegment(sketch, "E83", {"start": v(0.92, 23.83) * mm, "end": v(0.92, 23.13) * mm});
            skLineSegment(sketch, "E84", {"start": v(1.25, 25.28) * mm, "end": v(1.15, 25.12) * mm});
            skArc(sketch, "E85", {"start": v(1.15, 25.12) * mm, "mid": v(-0.49, 24.3) * mm, "end": v(0.92, 23.13) * mm});
            skLineSegment(sketch, "E86", {"start": v(1.62, 25.5) * mm, "end": v(1.62, 22.9) * mm});
            skLineSegment(sketch, "E87", {"start": v(1.62, 22.9) * mm, "end": v(1.82, 22.9) * mm});
            skLineSegment(sketch, "E88", {"start": v(1.82, 22.9) * mm, "end": v(1.82, 24.28) * mm});
            skLineSegment(sketch, "E89", {"start": v(1.82, 24.28) * mm, "end": v(2.47, 24.28) * mm});
            skLineSegment(sketch, "E90", {"start": v(2.47, 24.28) * mm, "end": v(2.47, 22.9) * mm});
            skLineSegment(sketch, "E91", {"start": v(2.47, 22.9) * mm, "end": v(2.65, 22.9) * mm});
            skLineSegment(sketch, "E92", {"start": v(2.65, 22.9) * mm, "end": v(2.65, 25.5) * mm});
            skLineSegment(sketch, "E93", {"start": v(2.65, 25.5) * mm, "end": v(2.47, 25.49) * mm});
            skLineSegment(sketch, "E94", {"start": v(2.47, 25.49) * mm, "end": v(2.47, 24.49) * mm});
            skLineSegment(sketch, "E95", {"start": v(2.47, 24.49) * mm, "end": v(1.82, 24.49) * mm});
            skLineSegment(sketch, "E96", {"start": v(1.82, 24.49) * mm, "end": v(1.82, 25.5) * mm});
            skLineSegment(sketch, "E97", {"start": v(1.82, 25.5) * mm, "end": v(1.62, 25.5) * mm});
            skLineSegment(sketch, "E98", {"start": v(3.74, 25.27) * mm, "end": v(3.36, 25.27) * mm});
            skLineSegment(sketch, "E99", {"start": v(3.74, 25.27) * mm, "end": v(3.74, 25.49) * mm});
            skLineSegment(sketch, "E100", {"start": v(3.74, 25.49) * mm, "end": v(2.82, 25.49) * mm});
            skLineSegment(sketch, "E101", {"start": v(2.82, 25.49) * mm, "end": v(2.82, 25.27) * mm});
            skLineSegment(sketch, "E102", {"start": v(2.82, 25.27) * mm, "end": v(3.2, 25.27) * mm});
            skLineSegment(sketch, "E103", {"start": v(3.2, 25.27) * mm, "end": v(3.2, 22.9) * mm});
            skLineSegment(sketch, "E104", {"start": v(3.2, 22.9) * mm, "end": v(3.38, 22.9) * mm});
            skLineSegment(sketch, "E105", {"start": v(3.38, 22.9) * mm, "end": v(3.36, 25.27) * mm});
            skSolve(sketch);
        }
        {
            var Q0;
            Q0=makeQuery(id+"F13.imprint","IMPRINT",FACE,{"disambiguationData":[TD([[makeQuery(id+"F13.imprint","IMPRINT",EDGE,{"derivedFrom":sQuery(id+"F13.wireOp",EDGE,"E53")}),1.0]])]});
            var Q1;
            Q1=makeQuery(id+"F13.imprint","IMPRINT",FACE,{"disambiguationData":[TD([[makeQuery(id+"F13.imprint","IMPRINT",EDGE,{"derivedFrom":sQuery(id+"F13.wireOp",EDGE,"E64")}),-1.0]])]});
            var Q2;
            Q2=makeQuery(id+"F13.imprint","IMPRINT",FACE,{"disambiguationData":[TD([[makeQuery(id+"F13.imprint","IMPRINT",EDGE,{"derivedFrom":sQuery(id+"F13.wireOp",EDGE,"E74")}),-1.0]])]});
            var Q3;
            Q3=makeQuery(id+"F13.imprint","IMPRINT",FACE,{"disambiguationData":[TD([[makeQuery(id+"F13.imprint","IMPRINT",EDGE,{"derivedFrom":sQuery(id+"F13.wireOp",EDGE,"E78")}),1.0]])]});
            var Q4;
            Q4=makeQuery(id+"F13.imprint","IMPRINT",FACE,{"disambiguationData":[TD([[makeQuery(id+"F13.imprint","IMPRINT",EDGE,{"derivedFrom":sQuery(id+"F13.wireOp",EDGE,"E86")}),1.0]])]});
            var Q5;
            Q5=makeQuery(id+"F13.imprint","IMPRINT",FACE,{"disambiguationData":[TD([[makeQuery(id+"F13.imprint","IMPRINT",EDGE,{"derivedFrom":sQuery(id+"F13.wireOp",EDGE,"E98")}),-1.0]])]});
            extrude(context, id + "F14", {"entities" : qUnion([Q0, Q1, Q2, Q3, Q4, Q5]), "operationType" : NewBodyOperationType.ADD, "endBound" : BoundingType.SYMMETRIC, "depth" : 0.64 * mm});
        }
        {
            var Q0;
            {var subQ0=sQuery(id+"F0.wireOp",EDGE,"E12");Q0=makeQuery(id+"F6.boolean.opBoolean","MERGE",FACE,{"derivedFrom":[makeQuery(id+"F1.opExtrude","CAP_FACE",FACE,{"disambiguationData":[OSD([sQuery(id+"F0.wireOp",EDGE,"E0"),sQuery(id+"F0.wireOp",EDGE,"E1"),sQuery(id+"F0.wireOp",EDGE,"E2"),sQuery(id+"F0.wireOp",EDGE,"E3"),sQuery(id+"F0.wireOp",EDGE,"E4"),sQuery(id+"F0.wireOp",EDGE,"E5"),sQuery(id+"F0.wireOp",EDGE,"E6"),sQuery(id+"F0.wireOp",EDGE,"E7"),sQuery(id+"F0.wireOp",EDGE,"E8"),sQuery(id+"F0.wireOp",EDGE,"E9"),sQuery(id+"F0.wireOp",EDGE,"E10"),sQuery(id+"F0.wireOp",EDGE,"E11"),subQ0,sQuery(id+"F0.wireOp",EDGE,"E13"),sQuery(id+"F0.wireOp",EDGE,"E14"),sQuery(id+"F0.wireOp",EDGE,"E15"),sQuery(id+"F0.wireOp",EDGE,"E16.filletArc"),sQuery(id+"F0.wireOp",EDGE,"E19"),sQuery(id+"F0.wireOp",EDGE,"E20"),sQuery(id+"F0.wireOp",EDGE,"E21"),sQuery(id+"F0.wireOp",EDGE,"E22")])],"isStart":false}),makeQuery(id+"F6.opExtrude","SWEPT_FACE",FACE,{"disambiguationData":[OSD([subQ0]),TDD([makeQuery(id+"F5.imprint","IMPRINT",EDGE,{"derivedFrom":makeQuery(id+"F1.opExtrude","CAP_EDGE",EDGE,{"disambiguationData":[OSD([subQ0])],"isStart":false})})])]})]});}
            var sketch = newSketch(context, id + "F15", { "sketchPlane" : qUnion([Q0])});
            skLineSegment(sketch, "E106", {"start": v(-40.82, 19.47) * mm, "end": v(-29.3, 19.5) * mm});
            skLineSegment(sketch, "E107", {"start": v(-29.3, 19.5) * mm, "end": v(-24.03, 14.45) * mm});
            skLineSegment(sketch, "E108", {"start": v(-24.03, 14.45) * mm, "end": v(-40.82, 14.45) * mm});
            skLineSegment(sketch, "E109", {"start": v(-40.82, 14.45) * mm, "end": v(-40.82, 19.47) * mm});
            skLineSegment(sketch, "E110", {"start": v(-41.63, 19.5) * mm, "end": v(-41.63, 14.45) * mm});
            skLineSegment(sketch, "E111", {"start": v(-41.63, 14.45) * mm, "end": v(-50.09, 14.45) * mm});
            skArc(sketch, "E112", {"start": v(-41.63, 19.5) * mm, "mid": v(-46.5, 18.06) * mm, "end": v(-50.09, 14.45) * mm});
            skSolve(sketch);
        }
        {
            var Q0;
            Q0=makeQuery(id+"F15.imprint","IMPRINT",FACE,{"disambiguationData":[TD([[makeQuery(id+"F15.imprint","IMPRINT",EDGE,{"derivedFrom":sQuery(id+"F15.wireOp",EDGE,"E110")}),-1.0]])]});
            var Q1;
            Q1=makeQuery(id+"F15.imprint","IMPRINT",FACE,{"disambiguationData":[TD([[makeQuery(id+"F15.imprint","IMPRINT",EDGE,{"derivedFrom":sQuery(id+"F15.wireOp",EDGE,"E106")}),-1.0]])]});
            extrude(context, id + "F16", {"entities" : qUnion([Q0, Q1]), "operationType" : NewBodyOperationType.REMOVE, "endBound" : BoundingType.UP_TO_NEXT, "oppositeDirection" : true, "depth" : 25.4 * mm});
        }
        {
            var Q0;
            Q0=makeQuery(id+"F16.boolean.opBoolean","COPY",FACE,{"derivedFrom":makeQuery(id+"F16.opExtrude","SWEPT_FACE",FACE,{"disambiguationData":[OSD([sQuery(id+"F15.wireOp",EDGE,"E109")])]})});
            var sketch = newSketch(context, id + "F17", { "sketchPlane" : qUnion([Q0])});
            skLineSegment(sketch, "E113.bottom", {"start": v(-17.78, 19.47) * mm, "end": v(17.78, 19.47) * mm});
            skLineSegment(sketch, "E113.top", {"start": v(-17.78, 14.45) * mm, "end": v(17.78, 14.45) * mm});
            skLineSegment(sketch, "E113.left", {"start": v(-17.78, 19.47) * mm, "end": v(-17.78, 14.45) * mm});
            skLineSegment(sketch, "E113.right", {"start": v(17.78, 19.47) * mm, "end": v(17.78, 14.45) * mm});
            skSolve(sketch);
        }
        {
            var Q0;
            Q0=makeQuery(id+"F17.imprint","IMPRINT",FACE,{"disambiguationData":[TD([[makeQuery(id+"F17.imprint","IMPRINT",EDGE,{"derivedFrom":sQuery(id+"F17.wireOp",EDGE,"E113.bottom")}),1.0]])]});
            extrude(context, id + "F18", {"entities" : qUnion([Q0]), "operationType" : NewBodyOperationType.REMOVE, "endBound" : BoundingType.UP_TO_NEXT, "oppositeDirection" : true, "depth" : 25.4 * mm});
        }
        {
            var Q0;
            Q0=makeQuery(id+"F1.opExtrude","SWEPT_EDGE",EDGE,{"disambiguationData":[OSD([sQuery(id+"F0.wireOp",EDGE,"E8"),sQuery(id+"F0.wireOp",EDGE,"E10")])]});
            fillet(context, id + "F19", {"entities" : qUnion([Q0]), "radius" : 0.75 * mm, "tangentPropagation" : true, "allowEdgeOverflow" : false});
        }
        {
            var Q0;
            Q0=makeQuery(id+"F6.opExtrude","CAP_EDGE",EDGE,{"disambiguationData":[OSD([sQuery(id+"F0.wireOp",EDGE,"E11"),sQuery(id+"F0.wireOp",EDGE,"E12")])],"isStart":false});
            fillet(context, id + "F20", {"entities" : qUnion([Q0]), "radius" : 23.36 * mm, "tangentPropagation" : true, "allowEdgeOverflow" : false});
        }
        {
            var Q0;
            {var subQ0=sQuery(id+"F0.wireOp",EDGE,"E12");var subQ1=sQuery(id+"F0.wireOp",EDGE,"E14");var subQ2=makeQuery(id+"F2.opFillet","BLEND_EDGE",EDGE,{"blendedFrom":[makeQuery(id+"F1.opExtrude","SWEPT_EDGE",EDGE,{"disambiguationData":[OSD([subQ0,subQ1])]}),makeQuery(id+"F1.opExtrude","SWEPT_FACE",FACE,{"disambiguationData":[OSD([subQ0])]})],"blendedInto":[makeQuery(id+"F1.opExtrude","SWEPT_FACE",FACE,{"disambiguationData":[OSD([subQ0])]})]});Q0=makeQuery(id+"F6.opExtrude","CAP_EDGE",EDGE,{"disambiguationData":[OSD([subQ0,subQ1]),TDD([makeQuery(id+"F5.imprint","IMPRINT",EDGE,{"disambiguationData":[TD([[makeQuery(id+"F5.imprint","INTERSECT",VERTEX,{"derivedFrom":[subQ2,makeQuery(id+"F1.opExtrude","CAP_EDGE",EDGE,{"disambiguationData":[OSD([subQ0])],"isStart":true})]}),1.0]])],"derivedFrom":subQ2})])],"isStart":false});}
            var Q1;
            {var subQ0=sQuery(id+"F0.wireOp",EDGE,"E12");var subQ1=sQuery(id+"F0.wireOp",EDGE,"E14");var subQ2=makeQuery(id+"F2.opFillet","BLEND_EDGE",EDGE,{"blendedFrom":[makeQuery(id+"F1.opExtrude","SWEPT_EDGE",EDGE,{"disambiguationData":[OSD([subQ0,subQ1])]}),makeQuery(id+"F1.opExtrude","SWEPT_FACE",FACE,{"disambiguationData":[OSD([subQ0])]})],"blendedInto":[makeQuery(id+"F1.opExtrude","SWEPT_FACE",FACE,{"disambiguationData":[OSD([subQ0])]})]});Q1=makeQuery(id+"F6.opExtrude","CAP_EDGE",EDGE,{"disambiguationData":[OSD([subQ0,subQ1]),TDD([makeQuery(id+"F5.imprint","IMPRINT",EDGE,{"disambiguationData":[TD([[makeQuery(id+"F5.imprint","INTERSECT",VERTEX,{"derivedFrom":[subQ2,makeQuery(id+"F1.opExtrude","CAP_EDGE",EDGE,{"disambiguationData":[OSD([subQ0])],"isStart":false})]}),-1.0]])],"derivedFrom":subQ2})])],"isStart":false});}
            fillet(context, id + "F21", {"entities" : qUnion([Q0, Q1]), "radius" : 5.08 * mm, "tangentPropagation" : true, "allowEdgeOverflow" : false});
        }
        {
            var Q0;
            Q0=makeQuery(id+"F1.opExtrude","CAP_EDGE",EDGE,{"disambiguationData":[OSD([sQuery(id+"F0.wireOp",EDGE,"E13")])],"isStart":false});
            var Q1;
            Q1=makeQuery(id+"F1.opExtrude","CAP_EDGE",EDGE,{"disambiguationData":[OSD([sQuery(id+"F0.wireOp",EDGE,"E13")])],"isStart":true});
            fillet(context, id + "F22", {"entities" : qUnion([Q0, Q1]), "radius" : 2.08 * mm, "tangentPropagation" : true, "allowEdgeOverflow" : false});
        }
        {
            var Q0;
            Q0=makeQuery(id+"F1.opExtrude","CAP_EDGE",EDGE,{"disambiguationData":[OSD([sQuery(id+"F0.wireOp",EDGE,"E1")])],"isStart":true});
            var Q1;
            Q1=makeQuery(id+"F1.opExtrude","CAP_EDGE",EDGE,{"disambiguationData":[OSD([sQuery(id+"F0.wireOp",EDGE,"E1")])],"isStart":false});
            fillet(context, id + "F23", {"entities" : qUnion([Q0, Q1]), "radius" : 3.25 * mm, "tangentPropagation" : true, "allowEdgeOverflow" : false});
        }
    });
